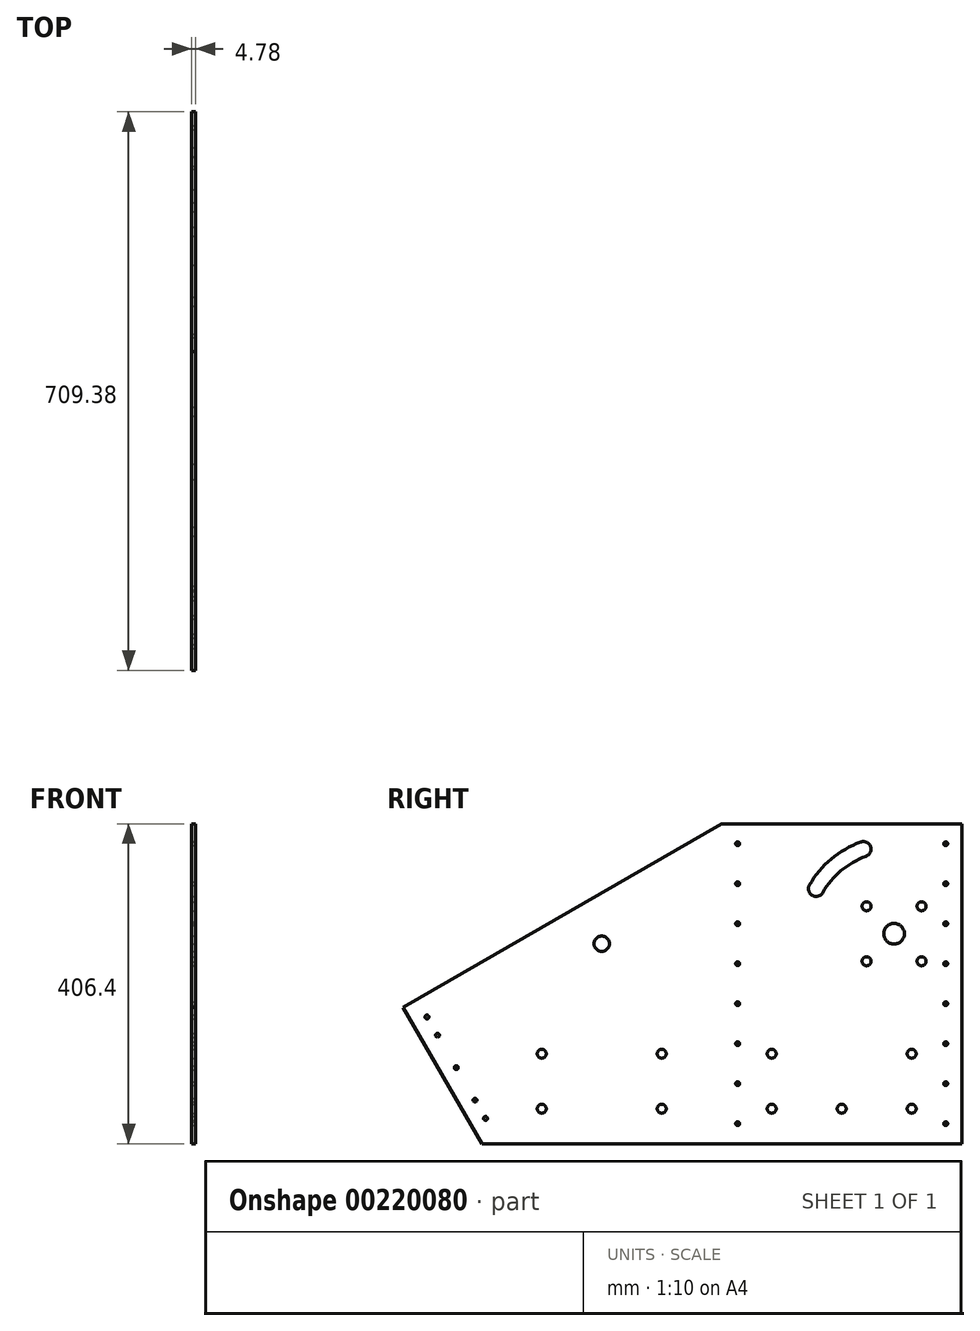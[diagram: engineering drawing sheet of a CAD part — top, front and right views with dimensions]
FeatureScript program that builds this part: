
annotation { "Feature Type Name" : "Feature", "Feature Type Description" : "" }
export const myFeature = defineFeature(function(context is Context, id is Id, definition is map)
    precondition{}
    {
        {
            var Q0;
            Q0=qCreatedBy(makeId("Right.planeOp"),FACE);
            var sketch = newSketch(context, id + "F0", { "sketchPlane" : qUnion([Q0])});
            skLineSegment(sketch, "E0.bottom", {"start": v(0, 0) * mm, "end": v(304.8, 0) * mm});
            skLineSegment(sketch, "E0.top", {"start": v(0, 406.4) * mm, "end": v(304.8, 406.4) * mm});
            skLineSegment(sketch, "E0.left", {"start": v(0, 0) * mm, "end": v(0, 406.4) * mm, "construction": true});
            skLineSegment(sketch, "E0.right", {"start": v(304.8, 0) * mm, "end": v(304.8, 406.4) * mm});
            skLineSegment(sketch, "E1", {"start": v(0, 406.4) * mm, "end": v(-404.58, 172.82) * mm});
            skLineSegment(sketch, "E2", {"start": v(-304.8, 230.42) * mm, "end": v(-304.8, 0) * mm, "construction": true});
            skLineSegment(sketch, "E3", {"start": v(-304.8, 0) * mm, "end": v(0, 0) * mm});
            skLineSegment(sketch, "E4", {"start": v(-304.8, 0) * mm, "end": v(-404.58, 172.82) * mm});
            skSolve(sketch);
        }
        {
            var Q0;
            Q0 = qSketchRegion(id + "F0", true);
            extrude(context, id + "F1", {"entities" : qUnion([Q0]), "oppositeDirection" : true, "depth" : 4.78 * mm});
        }
        {
            var Q0;
            Q0=makeQuery(id+"F1.opExtrude","CAP_FACE",FACE,{"disambiguationData":[OSD([sQuery(id+"F0.wireOp",EDGE,"E0.bottom"),sQuery(id+"F0.wireOp",EDGE,"E0.top"),sQuery(id+"F0.wireOp",EDGE,"E0.left"),sQuery(id+"F0.wireOp",EDGE,"E0.right")])],"isStart":true});
            var sketch = newSketch(context, id + "F2", { "sketchPlane" : qUnion([Q0])});
            skLineSegment(sketch, "E5.0.0", {"start": v(304.8, 406.4) * mm, "end": v(0, 406.4) * mm, "construction": true});
            skLineSegment(sketch, "E5.0.1", {"start": v(0, 406.4) * mm, "end": v(0, 0) * mm, "construction": true});
            skLineSegment(sketch, "E5.0.2", {"start": v(0, 0) * mm, "end": v(304.8, 0) * mm, "construction": true});
            skLineSegment(sketch, "E5.0.3", {"start": v(304.8, 0) * mm, "end": v(304.8, 406.4) * mm, "construction": true});
            skLineSegment(sketch, "E6", {"start": v(266.7, 430.78) * mm, "end": v(266.7, -45.45) * mm, "construction": true});
            skLineSegment(sketch, "E7", {"start": v(-67.57, 139.7) * mm, "end": v(404.97, 139.7) * mm, "construction": true});
            skCircle(sketch, "E8", {"center": v(218.95, 266.7) * mm, "radius": 13.1 * mm});
            skLineSegment(sketch, "E9.bottom", {"start": v(253.87, 301.63) * mm, "end": v(184.02, 301.63) * mm, "construction": true});
            skLineSegment(sketch, "E9.top", {"start": v(253.87, 231.78) * mm, "end": v(184.02, 231.78) * mm, "construction": true});
            skLineSegment(sketch, "E9.left", {"start": v(253.87, 301.63) * mm, "end": v(253.87, 231.78) * mm, "construction": true});
            skLineSegment(sketch, "E9.right", {"start": v(184.02, 301.63) * mm, "end": v(184.02, 231.78) * mm, "construction": true});
            skCircle(sketch, "E10", {"center": v(184.02, 301.63) * mm, "radius": 5.75 * mm});
            skCircle(sketch, "E11", {"center": v(253.87, 301.63) * mm, "radius": 5.75 * mm});
            skCircle(sketch, "E12", {"center": v(253.87, 231.78) * mm, "radius": 5.75 * mm});
            skCircle(sketch, "E13", {"center": v(184.02, 231.78) * mm, "radius": 5.75 * mm});
            skLineSegment(sketch, "E14", {"start": v(38.1, 422.67) * mm, "end": v(38.1, -17.9) * mm, "construction": true});
            skLineSegment(sketch, "E15.bottom", {"start": v(63.5, 114.3) * mm, "end": v(241.3, 114.3) * mm, "construction": true});
            skLineSegment(sketch, "E15.top", {"start": v(63.5, 44.45) * mm, "end": v(241.3, 44.45) * mm, "construction": true});
            skLineSegment(sketch, "E15.left", {"start": v(63.5, 114.3) * mm, "end": v(63.5, 44.45) * mm, "construction": true});
            skLineSegment(sketch, "E15.right", {"start": v(241.3, 114.3) * mm, "end": v(241.3, 44.45) * mm, "construction": true});
            skLineSegment(sketch, "E16", {"start": v(-12.3, 88.9) * mm, "end": v(332.7, 88.9) * mm, "construction": true});
            skCircle(sketch, "E17", {"center": v(63.5, 114.3) * mm, "radius": 5.75 * mm});
            skCircle(sketch, "E18", {"center": v(241.3, 114.3) * mm, "radius": 5.75 * mm});
            skCircle(sketch, "E19", {"center": v(241.3, 44.45) * mm, "radius": 5.75 * mm});
            skCircle(sketch, "E20", {"center": v(63.5, 44.45) * mm, "radius": 5.75 * mm});
            skCircle(sketch, "E21", {"center": v(152.4, 44.45) * mm, "radius": 5.75 * mm});
            skCircle(sketch, "E22", {"center": v(152.4, 114.3) * mm, "radius": 5.75 * mm, "construction": true});
            skSolve(sketch);
        }
        {
            var Q0;
            Q0 = qSketchRegion(id + "F2", true);
            extrude(context, id + "F3", {"entities" : qUnion([Q0]), "operationType" : NewBodyOperationType.REMOVE, "oppositeDirection" : true, "depth" : 25.4 * mm});
        }
        {
            var Q0;
            Q0=makeQuery(id+"F1.opExtrude","CAP_FACE",FACE,{"disambiguationData":[OSD([sQuery(id+"F0.wireOp",EDGE,"E0.bottom"),sQuery(id+"F0.wireOp",EDGE,"E0.top"),sQuery(id+"F0.wireOp",EDGE,"E0.left"),sQuery(id+"F0.wireOp",EDGE,"E0.right")])],"isStart":true});
            var sketch = newSketch(context, id + "F4", { "sketchPlane" : qUnion([Q0])});
            skCircle(sketch, "E23.0", {"center": v(218.95, 266.7) * mm, "radius": 13.1 * mm, "construction": true});
            skCircle(sketch, "E24", {"center": v(218.95, 266.7) * mm, "radius": 114.3 * mm, "construction": true});
            skLineSegment(sketch, "E25", {"start": v(218.95, 266.7) * mm, "end": v(218.95, 418.46) * mm, "construction": true});
            skLineSegment(sketch, "E26", {"start": v(218.95, 266.7) * mm, "end": v(154.47, 443.86) * mm, "construction": true});
            skLineSegment(sketch, "E27", {"start": v(218.95, 266.7) * mm, "end": v(148.2, 389.25) * mm, "construction": true});
            skLineSegment(sketch, "E28", {"start": v(218.95, 266.7) * mm, "end": v(133.6, 368.4) * mm, "construction": true});
            skLineSegment(sketch, "E29", {"start": v(218.95, 266.7) * mm, "end": v(104.85, 332.57) * mm, "construction": true});
            skArc(sketch, "E30", {"start": v(228.66, 380.59) * mm, "mid": v(228.67, 380.8) * mm, "end": v(228.67, 381) * mm});
            skCircle(sketch, "E31", {"center": v(179.86, 374.1) * mm, "radius": 6.54 * mm, "construction": true});
            skCircle(sketch, "E32", {"center": v(161.8, 365.69) * mm, "radius": 6.54 * mm, "construction": true});
            skCircle(sketch, "E33", {"center": v(145.48, 354.26) * mm, "radius": 6.54 * mm, "construction": true});
            skArc(sketch, "E34", {"start": v(111.54, 328.71) * mm, "mid": v(115.1, 315.43) * mm, "end": v(128.38, 318.99) * mm});
            skLineSegment(sketch, "E35", {"start": v(266.7, 416.6) * mm, "end": v(266.7, 256.88) * mm, "construction": true});
            skLineSegment(sketch, "E36", {"start": v(218.95, 266.7) * mm, "end": v(163.2, 419.87) * mm, "construction": true});
            skArc(sketch, "E37", {"start": v(183.18, 364.97) * mm, "mid": v(189, 377.43) * mm, "end": v(176.53, 383.24) * mm});
            skLineSegment(sketch, "E38", {"start": v(218.95, 381) * mm, "end": v(335.38, 381) * mm, "construction": true});
            skArc(sketch, "E39", {"start": v(183.18, 364.97) * mm, "mid": v(151.73, 346.81) * mm, "end": v(128.38, 318.99) * mm});
            skArc(sketch, "E40", {"start": v(176.53, 383.24) * mm, "mid": v(139.23, 361.7) * mm, "end": v(111.54, 328.71) * mm});
            skSolve(sketch);
        }
        {
            var Q0;
            Q0 = qSketchRegion(id + "F4", true);
            extrude(context, id + "F5", {"entities" : qUnion([Q0]), "operationType" : NewBodyOperationType.REMOVE, "oppositeDirection" : true, "depth" : 25.4 * mm});
        }
        {
            var Q0;
            Q0=makeQuery(id+"F1.opExtrude","CAP_FACE",FACE,{"disambiguationData":[OSD([sQuery(id+"F0.wireOp",EDGE,"E0.bottom"),sQuery(id+"F0.wireOp",EDGE,"E0.top"),sQuery(id+"F0.wireOp",EDGE,"E0.left"),sQuery(id+"F0.wireOp",EDGE,"E0.right")])],"isStart":true});
            var sketch = newSketch(context, id + "F6", { "sketchPlane" : qUnion([Q0])});
            skLineSegment(sketch, "E41", {"start": v(284.6, 413.06) * mm, "end": v(284.6, -22.82) * mm, "construction": true});
            skCircle(sketch, "E42", {"center": v(284.6, 25.4) * mm, "radius": 2.46 * mm});
            skCircle(sketch, "E43", {"center": v(284.6, 76.2) * mm, "radius": 2.46 * mm});
            skCircle(sketch, "E44", {"center": v(284.6, 127) * mm, "radius": 2.46 * mm});
            skCircle(sketch, "E45", {"center": v(284.6, 381) * mm, "radius": 2.46 * mm});
            skCircle(sketch, "E46", {"center": v(284.6, 177.8) * mm, "radius": 2.46 * mm});
            skCircle(sketch, "E47", {"center": v(284.6, 228.6) * mm, "radius": 2.46 * mm});
            skCircle(sketch, "E48", {"center": v(284.6, 279.4) * mm, "radius": 2.46 * mm});
            skCircle(sketch, "E49", {"center": v(284.6, 330.2) * mm, "radius": 2.46 * mm});
            skLineSegment(sketch, "E50", {"start": v(152.4, 406.4) * mm, "end": v(152.4, 0) * mm, "construction": true});
            skCircle(sketch, "E51.MirrorC", {"center": v(20.2, 25.4) * mm, "radius": 2.46 * mm});
            skCircle(sketch, "E52.MirrorC", {"center": v(20.2, 330.2) * mm, "radius": 2.46 * mm});
            skCircle(sketch, "E53.MirrorC", {"center": v(20.2, 76.2) * mm, "radius": 2.46 * mm});
            skCircle(sketch, "E54.MirrorC", {"center": v(20.2, 127) * mm, "radius": 2.46 * mm});
            skCircle(sketch, "E55.MirrorC", {"center": v(20.2, 177.8) * mm, "radius": 2.46 * mm});
            skCircle(sketch, "E56.MirrorC", {"center": v(20.2, 228.6) * mm, "radius": 2.46 * mm});
            skCircle(sketch, "E57.MirrorC", {"center": v(20.2, 279.4) * mm, "radius": 2.46 * mm});
            skCircle(sketch, "E58.MirrorC", {"center": v(20.2, 381) * mm, "radius": 2.46 * mm});
            skLineSegment(sketch, "E59.MirrorCS", {"start": v(20.2, 413.06) * mm, "end": v(20.2, -22.82) * mm, "construction": true});
            skLineSegment(sketch, "E60", {"start": v(0, 0) * mm, "end": v(0, 406.4) * mm, "construction": true});
            skLineSegment(sketch, "E61", {"start": v(0, 406.4) * mm, "end": v(48.43, 406.4) * mm, "construction": true});
            skLineSegment(sketch, "E62", {"start": v(-304.8, 0) * mm, "end": v(-241.61, 0) * mm, "construction": true});
            skCircle(sketch, "E63", {"center": v(-284.6, 25.4) * mm, "radius": 2.46 * mm, "construction": true});
            skLineSegment(sketch, "E64", {"start": v(-406.33, 216.24) * mm, "end": v(-263.7, -30.81) * mm, "construction": true});
            skCircle(sketch, "E65", {"center": v(-374.39, 160.92) * mm, "radius": 2.46 * mm});
            skCircle(sketch, "E66", {"center": v(-361.01, 137.75) * mm, "radius": 2.46 * mm});
            skCircle(sketch, "E67", {"center": v(-313.39, 55.26) * mm, "radius": 2.46 * mm});
            skCircle(sketch, "E68", {"center": v(-300.01, 32.1) * mm, "radius": 2.46 * mm});
            skLineSegment(sketch, "E69", {"start": v(-300.01, 32.1) * mm, "end": v(-330.35, 14.58) * mm, "construction": true});
            skLineSegment(sketch, "E70", {"start": v(-354.69, 86.4) * mm, "end": v(-303.18, 116.15) * mm, "construction": true});
            skCircle(sketch, "E71", {"center": v(-337.2, 96.5) * mm, "radius": 2.46 * mm});
            skSolve(sketch);
        }
        {
            var Q0;
            Q0 = qSketchRegion(id + "F6", true);
            extrude(context, id + "F7", {"entities" : qUnion([Q0]), "operationType" : NewBodyOperationType.REMOVE, "oppositeDirection" : true, "depth" : 25.4 * mm});
        }
        {
            var Q0;
            Q0=makeQuery(id+"F1.opExtrude","CAP_FACE",FACE,{"disambiguationData":[OSD([sQuery(id+"F0.wireOp",EDGE,"E0.bottom"),sQuery(id+"F0.wireOp",EDGE,"E0.top"),sQuery(id+"F0.wireOp",EDGE,"E0.right"),sQuery(id+"F0.wireOp",EDGE,"E1"),sQuery(id+"F0.wireOp",EDGE,"E2"),sQuery(id+"F0.wireOp",EDGE,"E3")])],"isStart":true});
            var sketch = newSketch(context, id + "F8", { "sketchPlane" : qUnion([Q0])});
            skLineSegment(sketch, "E72", {"start": v(63.5, 114.3) * mm, "end": v(-314.32, 114.3) * mm, "construction": true});
            skLineSegment(sketch, "E73", {"start": v(63.5, 44.45) * mm, "end": v(-324.42, 44.45) * mm, "construction": true});
            skCircle(sketch, "E74", {"center": v(-76.2, 114.3) * mm, "radius": 5.75 * mm});
            skCircle(sketch, "E75", {"center": v(-76.2, 44.45) * mm, "radius": 5.75 * mm});
            skCircle(sketch, "E76", {"center": v(-228.6, 114.3) * mm, "radius": 5.75 * mm});
            skCircle(sketch, "E77", {"center": v(-228.6, 44.45) * mm, "radius": 5.75 * mm});
            skCircle(sketch, "E78.0", {"center": v(241.3, 114.3) * mm, "radius": 5.75 * mm, "construction": true});
            skLineSegment(sketch, "E79", {"start": v(-152.4, 350.14) * mm, "end": v(-152.4, -41.84) * mm, "construction": true});
            skLineSegment(sketch, "E80", {"start": v(-228.6, 44.45) * mm, "end": v(-228.6, 309.8) * mm, "construction": true});
            skCircle(sketch, "E81", {"center": v(-152.4, 254) * mm, "radius": 9.73 * mm});
            skSolve(sketch);
        }
        {
            var Q0;
            Q0 = qSketchRegion(id + "F8", true);
            extrude(context, id + "F9", {"entities" : qUnion([Q0]), "operationType" : NewBodyOperationType.REMOVE, "oppositeDirection" : true, "depth" : 25.4 * mm});
        }
    });
